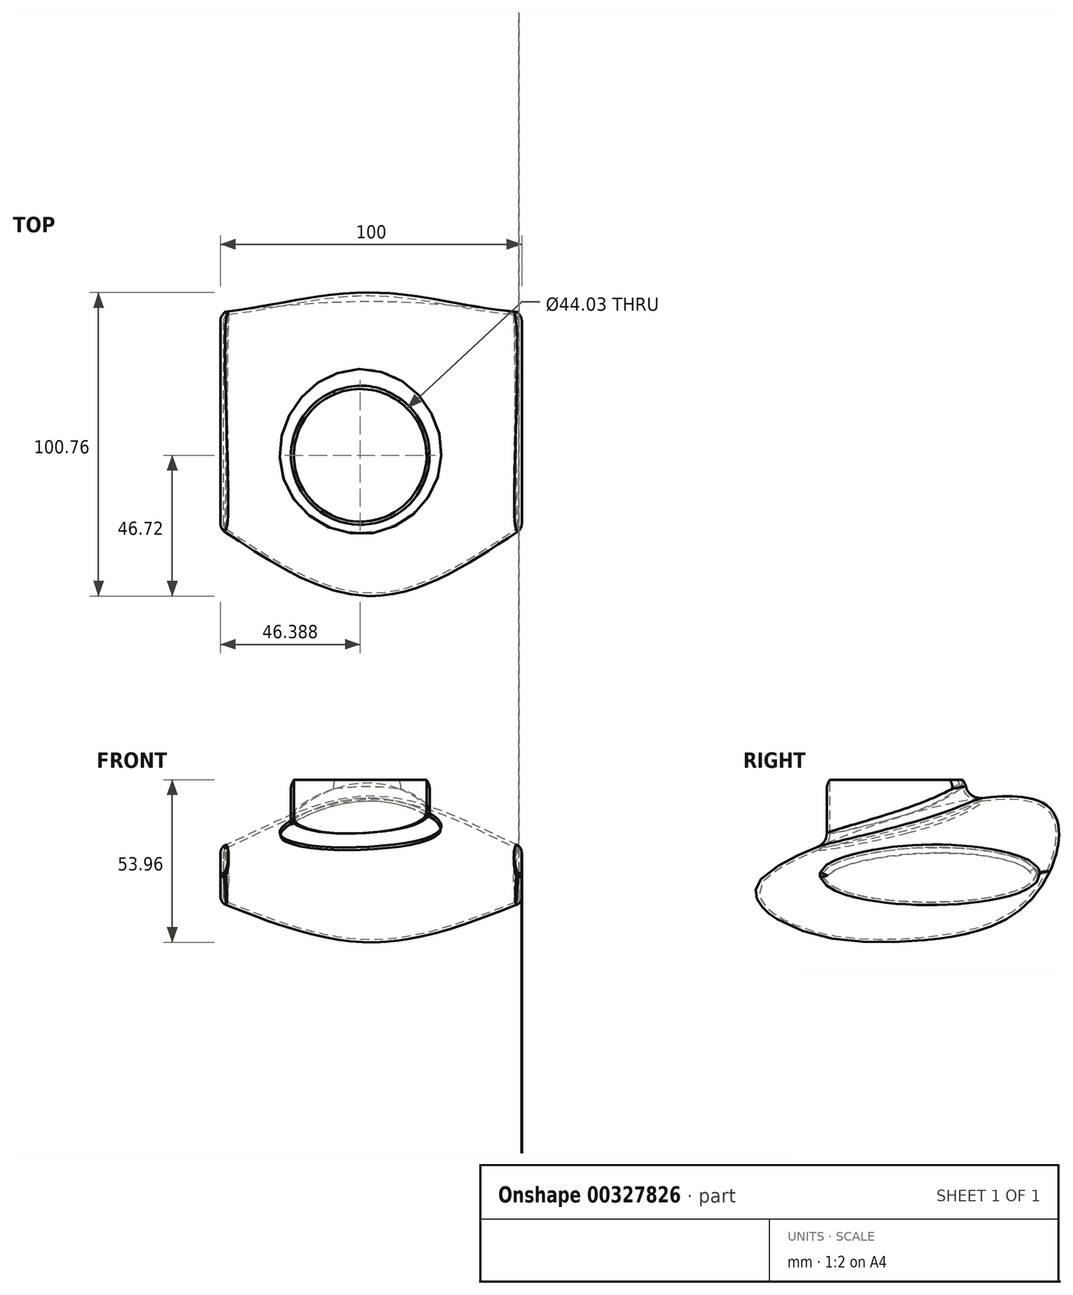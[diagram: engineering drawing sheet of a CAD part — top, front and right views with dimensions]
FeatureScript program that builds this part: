
annotation { "Feature Type Name" : "Feature", "Feature Type Description" : "" }
export const myFeature = defineFeature(function(context is Context, id is Id, definition is map)
    precondition{}
    {
        {
            var Q0;
            Q0=qCreatedBy(makeId("Right.planeOp"),FACE);
            var sketch = newSketch(context, id + "F0", { "sketchPlane" : qUnion([Q0])});
            skFitSpline(sketch, "E0", {"points": [v(-46.71, 0) * mm, v(-25.15, 15.63) * mm, v(50.16, 28.87) * mm, v(46.71, 0) * mm, v(13.65, -15.27) * mm, v(-31.98, -12.4) * mm, v(-46.71, 0) * mm]});
            skSolve(sketch);
        }
        {
            var Q0;
            Q0=qCreatedBy(makeId("Right.planeOp"),FACE);
            cPlane(context, id + "F1", {"entities" : qUnion([Q0]), "cplaneType" : CPlaneType.OFFSET, "offset" : 50 * mm, "width" : 150 * mm, "height" : 150 * mm});
        }
        {
            var Q0;
            Q0=qCreatedBy(makeId("Right.planeOp"),FACE);
            cPlane(context, id + "F2", {"entities" : qUnion([Q0]), "cplaneType" : CPlaneType.OFFSET, "offset" : 50 * mm, "oppositeDirection" : true, "width" : 150 * mm, "height" : 150 * mm});
        }
        {
            var Q0;
            Q0=qCreatedBy(id+"F1.planeOp",FACE);
            var sketch = newSketch(context, id + "F3", { "sketchPlane" : qUnion([Q0])});
            skEllipse(sketch, "E1", {"center": v(11.55, 5.95) * mm, "majorRadius": 35.95 * mm, "minorRadius": 9.27 * mm, "majorAxis": v(1, 0)});
            skSolve(sketch);
        }
        {
            var Q0;
            Q0=qCreatedBy(id+"F2.planeOp",FACE);
            var sketch = newSketch(context, id + "F4", { "sketchPlane" : qUnion([Q0])});
            skEllipse(sketch, "E2.0", {"center": v(11.55, 5.95) * mm, "majorRadius": 35.95 * mm, "minorRadius": 9.27 * mm, "majorAxis": v(1, 0)});
            skSolve(sketch);
        }
        {
            var Q0;
            Q0=makeQuery(id+"F3.imprint","IMPRINT",FACE,{"disambiguationData":[TD([[makeQuery(id+"F3.imprint","IMPRINT",EDGE,{"derivedFrom":sQuery(id+"F3.wireOp",EDGE,"E1")}),1.0]])]});
            var Q1;
            Q1=makeQuery(id+"F0.imprint","IMPRINT",FACE,{"disambiguationData":[TD([[makeQuery(id+"F0.imprint","IMPRINT",EDGE,{"derivedFrom":sQuery(id+"F0.wireOp",EDGE,"E0")}),-1.0]])]});
            var Q2;
            Q2=makeQuery(id+"F4.imprint","IMPRINT",FACE,{"disambiguationData":[TD([[makeQuery(id+"F4.imprint","IMPRINT",EDGE,{"derivedFrom":sQuery(id+"F4.wireOp",EDGE,"E2.0")}),1.0]])]});
            loft(context, id + "F5", {"sheetProfilesArray" : [{ "sheetProfileEntities" : qUnion([Q0]) }, { "sheetProfileEntities" : qUnion([Q1]) }, { "sheetProfileEntities" : qUnion([Q2]) }]});
        }
        {
            var Q0;
            Q0=makeQuery(id+"F5.opLoft","MID_CAP_EDGE",EDGE,{"disambiguationData":[OSD([sQuery(id+"F3.wireOp",EDGE,"E1")])],"capPos":0.0});
            var Q1;
            Q1=makeQuery(id+"F5.opLoft","MID_CAP_EDGE",EDGE,{"disambiguationData":[OSD([sQuery(id+"F3.wireOp",EDGE,"E1"),sQuery(id+"F4.wireOp",EDGE,"E2.0")])],"capPos":2.0});
            fillet(context, id + "F6", {"entities" : qUnion([Q0, Q1]), "radius" : 3 * mm, "tangentPropagation" : true, "allowEdgeOverflow" : false});
        }
        {
            var Q0;
            Q0=qCreatedBy(makeId("Top.planeOp"),FACE);
            cPlane(context, id + "F7", {"entities" : qUnion([Q0]), "cplaneType" : CPlaneType.OFFSET, "offset" : 25 * mm, "width" : 150 * mm, "height" : 150 * mm});
        }
        {
            var Q0;
            Q0=qCreatedBy(id+"F7.planeOp",FACE);
            var sketch = newSketch(context, id + "F8", { "sketchPlane" : qUnion([Q0])});
            skCircle(sketch, "E3", {"center": v(-3.61, 0) * mm, "radius": 23.01 * mm});
            skSolve(sketch);
        }
        {
            var Q0;
            Q0 = qSketchRegion(id + "F8", true);
            extrude(context, id + "F9", {"entities" : qUnion([Q0]), "operationType" : NewBodyOperationType.ADD, "endBound" : BoundingType.SYMMETRIC, "oppositeDirection" : true, "depth" : 25 * mm});
        }
        {
            var Q0;
            Q0=makeQuery(id+"F9.boolean.opBoolean","INTERSECT",EDGE,{"derivedFrom":[makeQuery(id+"F5.opLoft","SWEPT_FACE",FACE,{"disambiguationData":[OSD([sQuery(id+"F0.wireOp",EDGE,"E0"),sQuery(id+"F3.wireOp",EDGE,"E1")])]}),makeQuery(id+"F9.opExtrude","SWEPT_FACE",FACE,{"disambiguationData":[OSD([sQuery(id+"F8.wireOp",EDGE,"E3")])]})]});
            fillet(context, id + "F10", {"entities" : qUnion([Q0]), "radius" : 5 * mm, "tangentPropagation" : true, "allowEdgeOverflow" : false});
        }
        {
            var Q0;
            Q0=makeQuery(id+"F9.opExtrude","CAP_FACE",FACE,{"disambiguationData":[OSD([sQuery(id+"F8.wireOp",EDGE,"E3")])],"isStart":true});
            shell(context, id + "F11", {"entities" : qUnion([Q0]), "thickness" : 1 * mm});
        }
        {
            var Q0;
            Q0=makeQuery(id+"F9.opExtrude","CAP_EDGE",EDGE,{"disambiguationData":[OSD([sQuery(id+"F8.wireOp",EDGE,"E3")])],"isStart":true});
            fillet(context, id + "F12", {"entities" : qUnion([Q0]), "radius" : 5 * mm, "tangentPropagation" : true, "allowEdgeOverflow" : false});
        }
    });
